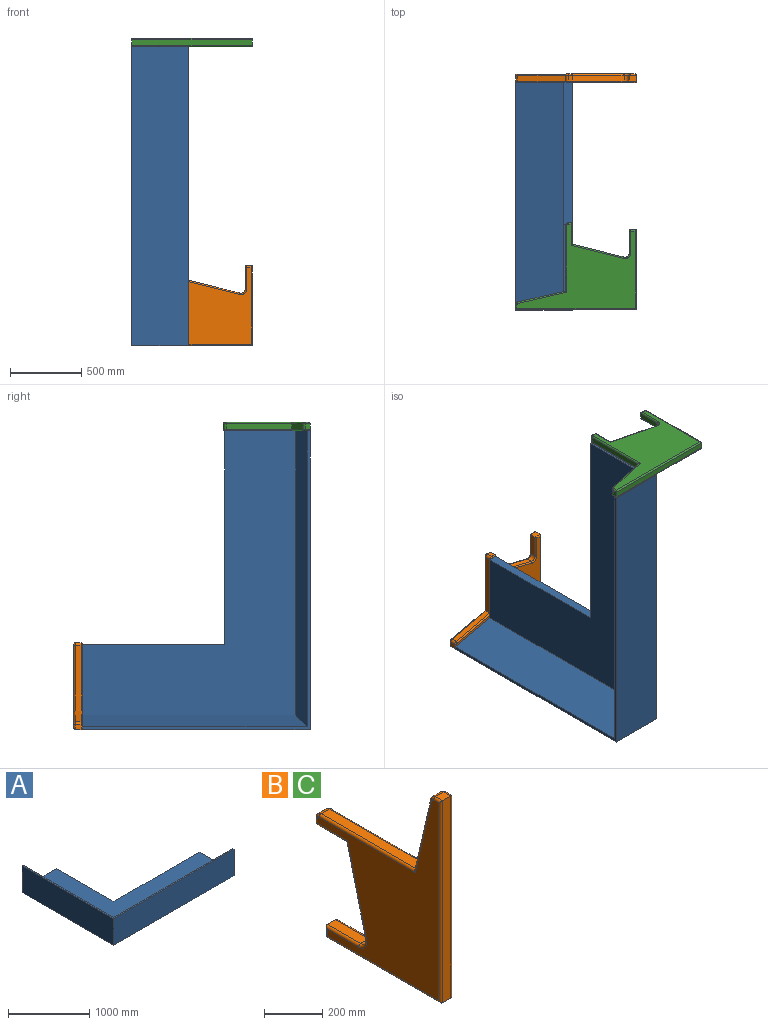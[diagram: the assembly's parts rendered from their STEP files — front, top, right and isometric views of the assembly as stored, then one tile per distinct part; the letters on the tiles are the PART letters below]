
ASSEMBLY  parts=3 mates=6
PART A: 11 faces, bbox 2100x1600x400 mm
  f0: plane 600x400mm, normal (1,0,0), area 56400mm2, adj f1,f4,f5,f8,f9,f10
  f1: plane 1500x60mm, normal (0,1,0), area 90000mm2, adj f0,f2,f4,f5
  f2: plane 1000x60mm, normal (1,0,0), area 60000mm2, adj f1,f3,f4,f5
  f3: plane 600x400mm, normal (0,1,0), area 56400mm2, adj f2,f4,f5,f6,f7,f9
  f4: plane 2000x1500mm, normal (0,0,1), area 1500000mm2, adj f0,f1,f2,f3,f7,f8
  f5: plane 2100x1600mm, normal (0,0,-1), area 1860000mm2, adj f0,f1,f2,f3,f6,f10
  f6: plane 1600x400mm, normal (-1,0,0), area 640000mm2, adj f3,f5,f9,f10
  f7: plane 1580x340mm, normal (0.97,0,0.23), area 537898.9mm2, adj f3,f4,f8,f9
  f8: plane 2080x340mm, normal (0,0.97,0.23), area 712541.4mm2, adj f0,f4,f7,f9
  f9: plane 2100x1600mm, normal (0,0,1), area 73600mm2, adj f0,f3,f6,f7,f8,f10
  f10: plane 2100x400mm, normal (0,-1,0), area 840000mm2, adj f0,f5,f6,f9
PART B: 41 faces, bbox 60x611.6x851.6 mm
  f0: plane 560x40.2mm, normal (0,0,-1), area 22512mm2, adj f1,f9,f16,f28
  f1: plane 50x40.2mm, normal (0,1,0), area 2010mm2, adj f0,f2,f15,f29
  f2: plane 161.58x40.2mm, normal (0,0,1), area 6495.4mm2, adj f1,f12,f17,f31
  f3: plane 362.72x90.68mm, normal (0,0.97,-0.24), area 15030.3mm2, adj f4,f12,f21,f35
  f4: plane 150x40.2mm, normal (0,0,-1), area 6030mm2, adj f3,f5,f23,f37
  f5: plane 40.2x30mm, normal (0,1,0), area 1206mm2, adj f4,f13,f25,f39
  f6: plane 460x40.2mm, normal (0,0,1), area 18492mm2, adj f7,f13,f26,f38
  f7: plane 334.46x76.45mm, normal (0,0.97,0.22), area 13791.9mm2, adj f6,f14,f24,f36
  f8: plane 40.2x34.06mm, normal (0,0,1), area 1369mm2, adj f9,f14,f20,f32
  f9: plane 850x40.2mm, normal (0,-1,0), area 34170mm2, adj f0,f8,f18,f30
  f10: plane 830.2x590.2mm, normal (1,0,0), area 223647.9mm2, adj f15,f16,f17,f18,f19,f20,f21,f22
  f11: plane 830.2x590.2mm, normal (-1,0,0), area 223647.9mm2, adj f28,f29,f30,f31,f32,f33,f34,f35
  f12: cylinder r=30mm len=40.2mm, axis (1,0,0), area 2189.8mm2, adj f2,f3,f19,f33
  f13: cylinder r=20mm len=40.2mm, axis (-1,0,0), area 1262.9mm2, adj f5,f6,f27,f40
  f14: cylinder r=20mm len=40.2mm, axis (-1,0,0), area 1082.3mm2, adj f7,f8,f22,f34
  f15: cylinder r=9.9mm len=50mm, axis (0,0,-1), area 665.7mm2, adj f1,f10,f16,f17
  f16: cylinder r=9.9mm len=560mm, axis (0,-1,0), area 8596.6mm2, adj f0,f10,f15,f18
  f17: cylinder r=9.9mm len=161.58mm, axis (0,1,0), area 2456.7mm2, adj f2,f10,f15,f19
  f18: cylinder r=9.9mm len=850mm, axis (0,0,1), area 13106.4mm2, adj f9,f10,f16,f20
  f19: torus R=39.9mm, axis (1,0,0), area 948.7mm2, adj f10,f12,f17,f21
  f20: cylinder r=9.9mm len=34.06mm, axis (0,1,0), area 473.7mm2, adj f8,f10,f18,f22
  f21: cylinder r=9.9mm len=372.62mm, axis (0,-0.24,-0.97), area 5858mm2, adj f3,f10,f19,f23
  f22: torus R=10.1mm, axis (1,0,0), area 343.4mm2, adj f10,f14,f20,f24
  f23: cylinder r=9.9mm len=157.73mm, axis (0,-1,0), area 2320.4mm2, adj f4,f10,f21,f25
  f24: cylinder r=9.9mm len=344.36mm, axis (0,0.22,-0.97), area 5379.8mm2, adj f7,f10,f22,f26
  f25: cylinder r=9.9mm len=30mm, axis (0,0,-1), area 410.6mm2, adj f5,f10,f23,f27
  f26: cylinder r=9.9mm len=467.89mm, axis (0,1,0), area 7198mm2, adj f6,f10,f24,f27
  f27: torus R=10.1mm, axis (1,0,0), area 400.7mm2, adj f10,f13,f25,f26
  f28: cylinder r=9.9mm len=560mm, axis (0,1,0), area 8596.6mm2, adj f0,f11,f29,f30
  f29: cylinder r=9.9mm len=50mm, axis (0,0,1), area 665.7mm2, adj f1,f11,f28,f31
  f30: cylinder r=9.9mm len=850mm, axis (0,0,-1), area 13106.4mm2, adj f9,f11,f28,f32
  f31: cylinder r=9.9mm len=161.58mm, axis (0,-1,0), area 2456.7mm2, adj f2,f11,f29,f33
  f32: cylinder r=9.9mm len=34.06mm, axis (0,-1,0), area 473.7mm2, adj f8,f11,f30,f34
  f33: torus R=39.9mm, axis (1,0,0), area 948.7mm2, adj f11,f12,f31,f35
  f34: torus R=10.1mm, axis (1,0,0), area 343.4mm2, adj f11,f14,f32,f36
  f35: cylinder r=9.9mm len=372.62mm, axis (0,0.24,0.97), area 5858mm2, adj f3,f11,f33,f37
  f36: cylinder r=9.9mm len=344.36mm, axis (0,-0.22,0.97), area 5379.8mm2, adj f7,f11,f34,f38
  f37: cylinder r=9.9mm len=157.73mm, axis (0,1,0), area 2320.4mm2, adj f4,f11,f35,f39
  f38: cylinder r=9.9mm len=467.89mm, axis (0,-1,0), area 7198mm2, adj f6,f11,f36,f40
  f39: cylinder r=9.9mm len=30mm, axis (0,0,1), area 410.6mm2, adj f5,f11,f37,f40
  f40: torus R=10.1mm, axis (1,0,0), area 400.7mm2, adj f11,f13,f38,f39
PART C: same geometry as B
PLACE A rot(axis=(0,-1,0),90deg) t=(-4347.65,2022.94,2002.78)mm
PLACE B rot(axis=(0.58,-0.58,-0.58),120deg) t=(-3897.65,3582.94,462.78)mm
PLACE C rot(axis=(0,-1,0),90deg) t=(-3897.65,2482.94,2002.78)mm
MATE planar C.f0 <-> B.f0  axis (1,0,0) through (-3897.65,2202.94,2032.78)mm
MATE planar A.f6 <-> B.f9  axis (0,0,-1) through (-4547.65,2722.94,-97.22)mm
MATE planar A.f0 <-> C.f11  axis (0,0,1) through (-4436.32,2126.89,2002.78)mm
MATE planar B.f10 <-> A.f3  axis (0,-1,0) through (-4198.73,3522.94,104.81)mm
MATE planar C.f9 <-> A.f10  axis (0,-1,0) through (-4322.65,1922.94,2032.78)mm
MATE planar C.f4 <-> A.f5  axis (1,0,0) through (-4347.65,2457.94,2032.78)mm
